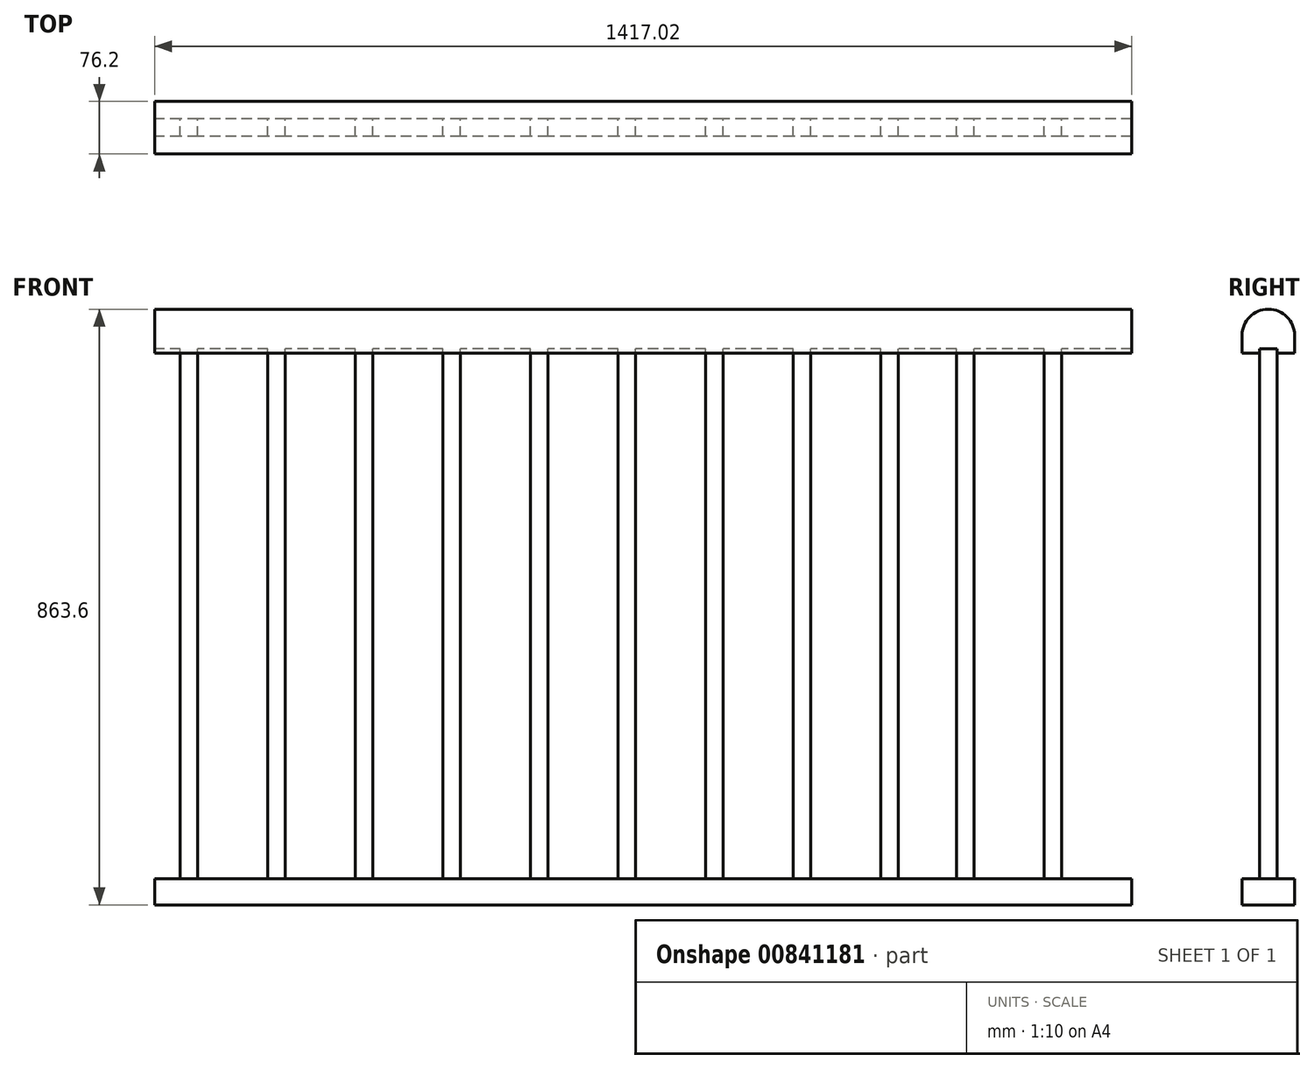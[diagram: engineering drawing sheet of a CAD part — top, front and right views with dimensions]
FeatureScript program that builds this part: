
annotation { "Feature Type Name" : "Feature", "Feature Type Description" : "" }
export const myFeature = defineFeature(function(context is Context, id is Id, definition is map)
    precondition{}
    {
        {
            var Q0;
            Q0=qCreatedBy(makeId("Right.planeOp"),FACE);
            var sketch = newSketch(context, id + "F0", { "sketchPlane" : qUnion([Q0])});
            skLineSegment(sketch, "E0.top", {"start": v(0, -25.4) * mm, "end": v(25.4, -25.4) * mm});
            skLineSegment(sketch, "E0.left", {"start": v(0, 0) * mm, "end": v(0, -25.4) * mm});
            skLineSegment(sketch, "E0.right", {"start": v(76.2, 0) * mm, "end": v(76.2, -25.4) * mm});
            skArc(sketch, "E1", {"start": v(76.2, 0) * mm, "mid": v(38.1, 38.1) * mm, "end": v(0, 0) * mm});
            skLineSegment(sketch, "E2", {"start": v(50.8, -25.4) * mm, "end": v(50.8, -19.05) * mm});
            skLineSegment(sketch, "E3", {"start": v(50.8, -19.05) * mm, "end": v(25.4, -19.05) * mm});
            skLineSegment(sketch, "E4", {"start": v(25.4, -19.05) * mm, "end": v(25.4, -25.4) * mm});
            skLineSegment(sketch, "E5.trimOffspring", {"start": v(50.8, -25.4) * mm, "end": v(76.2, -25.4) * mm});
            skLineSegment(sketch, "E6.bottom", {"start": v(0, -787.4) * mm, "end": v(76.2, -787.4) * mm});
            skLineSegment(sketch, "E6.top", {"start": v(0, -825.5) * mm, "end": v(76.2, -825.5) * mm});
            skLineSegment(sketch, "E6.left", {"start": v(0, -787.4) * mm, "end": v(0, -825.5) * mm});
            skLineSegment(sketch, "E6.right", {"start": v(76.2, -787.4) * mm, "end": v(76.2, -825.5) * mm});
            skSolve(sketch);
        }
        {
            var Q0;
            Q0=makeQuery(id+"F0.imprint","IMPRINT",FACE,{"disambiguationData":[TD([[makeQuery(id+"F0.imprint","IMPRINT",EDGE,{"derivedFrom":sQuery(id+"F0.wireOp",EDGE,"E0.top")}),1.0]])]});
            var Q1;
            Q1=makeQuery(id+"F0.imprint","IMPRINT",FACE,{"disambiguationData":[TD([[makeQuery(id+"F0.imprint","IMPRINT",EDGE,{"derivedFrom":sQuery(id+"F0.wireOp",EDGE,"E6.bottom")}),-1.0]])]});
            extrude(context, id + "F1", {"entities" : qUnion([Q0, Q1]), "depth" : 1417.02 * mm, "offsetDistance" : 25.4 * mm});
        }
        {
            var Q0;
            Q0=makeQuery(id+"F1.opExtrude","SWEPT_FACE",FACE,{"disambiguationData":[OSD([sQuery(id+"F0.wireOp",EDGE,"E3")])]});
            var sketch = newSketch(context, id + "F2", { "sketchPlane" : qUnion([Q0])});
            skLineSegment(sketch, "E7.bottom", {"start": v(1315.42, -25.4) * mm, "end": v(1290.02, -25.4) * mm});
            skLineSegment(sketch, "E7.top", {"start": v(1315.42, -50.8) * mm, "end": v(1290.02, -50.8) * mm});
            skLineSegment(sketch, "E7.right", {"start": v(1315.42, -25.4) * mm, "end": v(1315.42, -50.8) * mm});
            skLineSegment(sketch, "E8", {"start": v(1290.02, -25.4) * mm, "end": v(1290.02, -50.8) * mm});
            skLineSegment(sketch, "E9.bottom", {"start": v(1163.02, -25.4) * mm, "end": v(1188.42, -25.4) * mm});
            skLineSegment(sketch, "E9.top", {"start": v(1163.02, -50.8) * mm, "end": v(1188.42, -50.8) * mm});
            skLineSegment(sketch, "E9.left", {"start": v(1163.02, -25.4) * mm, "end": v(1163.02, -50.8) * mm});
            skLineSegment(sketch, "E9.right", {"start": v(1188.42, -25.4) * mm, "end": v(1188.42, -50.8) * mm});
            skLineSegment(sketch, "E10.bottom", {"start": v(1053.3, -25.4) * mm, "end": v(1078.7, -25.4) * mm});
            skLineSegment(sketch, "E10.top", {"start": v(1053.3, -50.8) * mm, "end": v(1078.7, -50.8) * mm});
            skLineSegment(sketch, "E10.left", {"start": v(1053.3, -25.4) * mm, "end": v(1053.3, -50.8) * mm});
            skLineSegment(sketch, "E10.right", {"start": v(1078.7, -25.4) * mm, "end": v(1078.7, -50.8) * mm});
            skLineSegment(sketch, "E11.bottom", {"start": v(926.3, -25.4) * mm, "end": v(951.7, -25.4) * mm});
            skLineSegment(sketch, "E11.top", {"start": v(926.3, -50.8) * mm, "end": v(951.7, -50.8) * mm});
            skLineSegment(sketch, "E11.left", {"start": v(926.3, -25.4) * mm, "end": v(926.3, -50.8) * mm});
            skLineSegment(sketch, "E11.right", {"start": v(951.7, -25.4) * mm, "end": v(951.7, -50.8) * mm});
            skLineSegment(sketch, "E12.bottom", {"start": v(799.3, -25.4) * mm, "end": v(824.7, -25.4) * mm});
            skLineSegment(sketch, "E12.top", {"start": v(799.3, -50.8) * mm, "end": v(824.7, -50.8) * mm});
            skLineSegment(sketch, "E12.left", {"start": v(799.3, -25.4) * mm, "end": v(799.3, -50.8) * mm});
            skLineSegment(sketch, "E12.right", {"start": v(824.7, -25.4) * mm, "end": v(824.7, -50.8) * mm});
            skLineSegment(sketch, "E13.bottom", {"start": v(545.3, -25.4) * mm, "end": v(570.7, -25.4) * mm});
            skLineSegment(sketch, "E13.top", {"start": v(545.3, -50.8) * mm, "end": v(570.7, -50.8) * mm});
            skLineSegment(sketch, "E13.left", {"start": v(545.3, -25.4) * mm, "end": v(545.3, -50.8) * mm});
            skLineSegment(sketch, "E13.right", {"start": v(570.7, -25.4) * mm, "end": v(570.7, -50.8) * mm});
            skLineSegment(sketch, "E14.bottom", {"start": v(672.3, -25.4) * mm, "end": v(697.7, -25.4) * mm});
            skLineSegment(sketch, "E14.top", {"start": v(672.3, -50.8) * mm, "end": v(697.7, -50.8) * mm});
            skLineSegment(sketch, "E14.left", {"start": v(672.3, -25.4) * mm, "end": v(672.3, -50.8) * mm});
            skLineSegment(sketch, "E14.right", {"start": v(697.7, -25.4) * mm, "end": v(697.7, -50.8) * mm});
            skLineSegment(sketch, "E15.bottom", {"start": v(418.3, -25.4) * mm, "end": v(443.7, -25.4) * mm});
            skLineSegment(sketch, "E15.top", {"start": v(418.3, -50.8) * mm, "end": v(443.7, -50.8) * mm});
            skLineSegment(sketch, "E15.left", {"start": v(418.3, -25.4) * mm, "end": v(418.3, -50.8) * mm});
            skLineSegment(sketch, "E15.right", {"start": v(443.7, -25.4) * mm, "end": v(443.7, -50.8) * mm});
            skLineSegment(sketch, "E16.bottom", {"start": v(291.3, -25.4) * mm, "end": v(316.7, -25.4) * mm});
            skLineSegment(sketch, "E16.top", {"start": v(291.3, -50.8) * mm, "end": v(316.7, -50.8) * mm});
            skLineSegment(sketch, "E16.left", {"start": v(291.3, -25.4) * mm, "end": v(291.3, -50.8) * mm});
            skLineSegment(sketch, "E16.right", {"start": v(316.7, -25.4) * mm, "end": v(316.7, -50.8) * mm});
            skLineSegment(sketch, "E17.bottom", {"start": v(164.3, -25.4) * mm, "end": v(189.7, -25.4) * mm});
            skLineSegment(sketch, "E17.top", {"start": v(164.3, -50.8) * mm, "end": v(189.7, -50.8) * mm});
            skLineSegment(sketch, "E17.left", {"start": v(164.3, -25.4) * mm, "end": v(164.3, -50.8) * mm});
            skLineSegment(sketch, "E17.right", {"start": v(189.7, -25.4) * mm, "end": v(189.7, -50.8) * mm});
            skLineSegment(sketch, "E18.bottom", {"start": v(37.3, -25.4) * mm, "end": v(62.7, -25.4) * mm});
            skLineSegment(sketch, "E18.top", {"start": v(37.3, -50.8) * mm, "end": v(62.7, -50.8) * mm});
            skLineSegment(sketch, "E18.left", {"start": v(37.3, -25.4) * mm, "end": v(37.3, -50.8) * mm});
            skLineSegment(sketch, "E18.right", {"start": v(62.7, -25.4) * mm, "end": v(62.7, -50.8) * mm});
            skSolve(sketch);
        }
        {
            var Q0;
            Q0=qSketchRegion(id+"F2",true);
            var Q1;
            Q1=makeQuery(id+"F1.opExtrude","SWEPT_FACE",FACE,{"disambiguationData":[OSD([sQuery(id+"F0.wireOp",EDGE,"E6.bottom")])]});
            extrude(context, id + "F3", {"entities" : qUnion([Q0, Q1]), "operationType" : NewBodyOperationType.ADD, "endBound" : BoundingType.UP_TO_NEXT, "depth" : 25.4 * mm, "offsetDistance" : 25.4 * mm});
        }
    });
